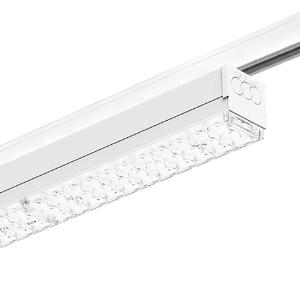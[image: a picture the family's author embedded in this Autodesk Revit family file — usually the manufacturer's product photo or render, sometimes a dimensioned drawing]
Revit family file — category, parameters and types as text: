
# Revit family: 3f_filippi_-_3f_zeta_track_l_ampio_3f_filippi_-_47136_-_3f_zeta_tk_l_15_ampio_l605
name_source: partatom
category: Lighting Fixtures
units: mm (PartAtom-declared; Revit-internal decimal feet)

## family parameters
Cut with Voids When Loaded = No
Host = Face
Light Source = No
Part Type = Normal
Room Calculation Point = No
Round Connector Dimension = Use Diameter
Shared = No

## types (1)
- 3F Filippi - 3F Zeta Track L Ampio (1 x LED, 2749 lm, 17 W, 4000 K)
    Apparent Load = 17 VA
    Approval mark = CE
    CIE Flux Codes = 61 95 99 99 100
    Color Rendering = 80
    Color Temperature = 4000 K
    Control Gear = Electronic ballast
    Default Elevation = 1800 mm
    Description = ILLUMINOTECHNICAL
Luminous efficiency 100% (DLOR 99%, ULOR 1%).
Initial luminous flux of the luminaire 2749 lm.
Symmetric wide direct distribution.
Installation Interdistance Transv.D = 1.39 x hu - Long.D = 1.43 x hu.
Tabular UGR (CIE 117 - 4H-8H; S=0.25H; 70/50/20): RUG 21.6 - 22.3.
Beam angle: 102° - 103°.
Luminous efficacy 162 lm/W.
Lifetime (L93/B10): 30000 h. (tq+25°C)
Lifetime (L90/B10): 50000 h. (tq+25°C)
Lifetime (L85/B10): 80000 h. (tq+25°C)
Lifetime (L80/B10): 100000 h. (tq+25°C)
Sudden decreased luminous flux after 50000 hours: 0% (C0).
Photobiological safety in compliance with IEC/TR 62778: RG0 risk exempt, (IEC 62471).
In compliance with IEC/EN 62722-2-1 - IEC/EN 62717 standards.

SOURCE
Linear LED module 15W/840.
Energy efficiency class (UE 2019/2020 - UE 2019/2015): C.
CIE 13.3 Colour rendering index: CRI >80 (R9 <50%).
IES TM-30 Fidelity Index: Rf = 84 Rg = 95.
CCT nominal colour temperature 4000 K.
Colour initial tolerance (MacAdam): SDCM 3.

MECHANICAL
Housing in hot-galvanised steel, painted in white polyester, obtained through rolling process with adapters to busbar in white polycarbonate.
Mechanical truck adapter.
Light unit in hot-galvanised steel, painted in white polyester base with fixing springs and retractable safety hooks in stainless steel.
Lenses for wide distribution, in transparent methacrylate (PMMA) with external flat surface.
End caps in white polycarbonate.
Luminaire with limited surface temperature. - D - (EN 60598-2-24)
Dimensions: 605x62 mm, height 67 mm. Weight 1.39 kg.
IP40 protection degree.
Mechanical strength to impacts IK06 (1 joule).
Glow-wire test resistance 650°C.

ELECTRICAL
Halogen Free electronic wiring 230V-50/60Hz, power factor 0.85, THD <25%, constant output current, class I, 1 driver.
Power of the luminaire 17 W.
ENEC - CE.
SAFE FLICKER: PstLM=<1 and SVM=<0.4 (IEC TR 61547-1 and IEC TR 63158), to ensure a more comfortable and safe light.
Ambient temperature from 0°C to +25°C.
Temperature class T6 max 85°C.
Truck adapter, 4-way.
Relative humidity UR: <85%.

INSTALLATION
Track.
This product is suitable for installation on a 3-phase electrified busbar "Binario 3F".

APPLICATIONS
Environments: architectural, commercial, transit areas, cornices, boards.

WARNING
Luminaire designed for disposal/recycling at end-of-life.
Replaceable (LED only) light source by a professional. Replaceable control gear by a professional.
    Height = 67 mm
    Lamp = 1 x LED
    Lamp Light Flux = 2749 lm
    Lamp Power = 17 W
    Lamp count = 1
    Length = 605 mm
    Lifetime = 50000 h
    Luminous efficacy = 162 lm/W
    Manufacturer = 3F Filippi
    ModVariant = No
    Model = 3F Filippi - 47136 - 3F Zeta TK L 15 AMPIO L605
    Mounting Place = Ceiling
    Mounting Type = Rail mounted
    Number of Poles = 1
    OnlyDefault = Yes
    Power Factor = 1
    Product Name = 3F Filippi - 3F Zeta Track L Ampio
    Product group = track mounted spotlight
    ProductGroupID = 12
    Protection Class = Protection class I
    Protection Degree = IP 40
    RLX_Detail_Level = 1
    RLX_Emergency_Light_Flux = 0 lm
    RLX_Emergency_Type = 0
    RLX_Emergency_Type_DB = No
    RlxData = <blob elided: 131929 chars, md5=c65b30e9>
    Socket = socket
    Standby Power = 0 W
    System Light Flux = 2749 lm
    System Power = 17 W
    Type Comments = Product without accessories
    Type Image = 3ffilippi_3f_zeta_track_l_ampio.jpg
    URL = http://relux.com
    VarID = ---
    Voltage = 0 V
    Weight = 0.00 kg
    Width = 62 mm  [stored 0.203412 ft]

note: [stored X ft] marks values corroborated as IEEE doubles in the binary element streams (Revit-internal decimal feet)

## geometry (parser evidence)
native form markers: Blend x4, Sweep x10
no freeform markers — native parametric forms only
